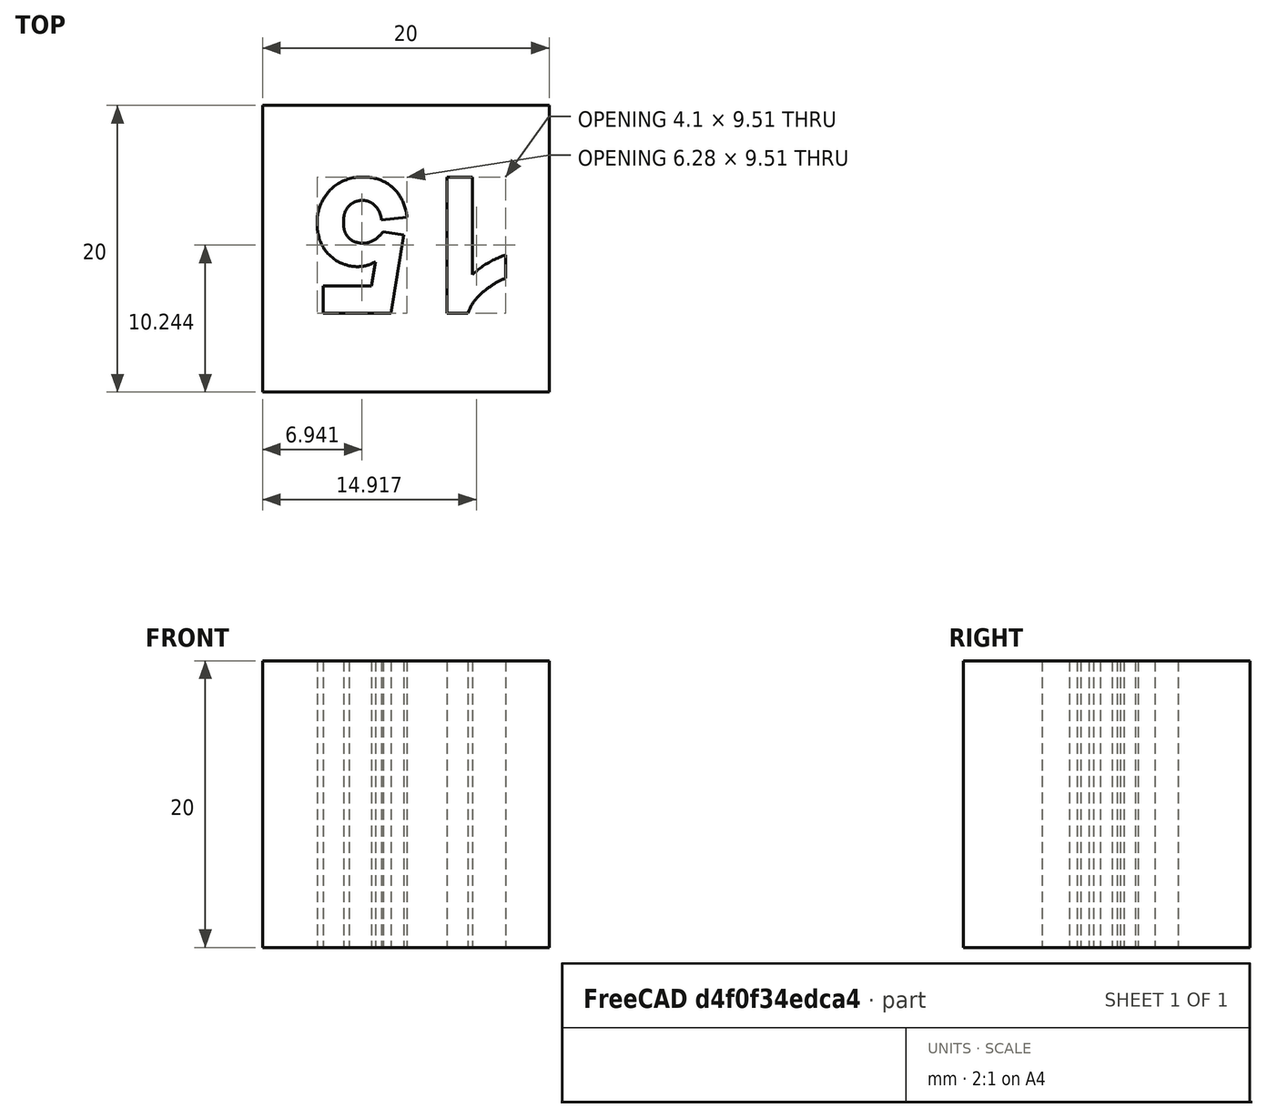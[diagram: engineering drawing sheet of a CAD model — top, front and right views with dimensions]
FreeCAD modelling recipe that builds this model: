
FCSTD DOCUMENT  (FreeCAD 0.18R16131 (Git))
Label: fill
License: All rights reserved
LicenseURL: http://en.wikipedia.org/wiki/All_rights_reserved
objects: Part::Box×1, Part::Part2DObjectPython×1, Part::Extrusion×1, Part::Cut×1
note: 4 computed .brp shape members not serialized (recipe doc carries the construction recipe); baked Part::Feature solids carry a one-line shape summary decoded from their .brp

FEATURE [Part::Box] Box  label="Cube"
  AttacherType = Attacher::AttachEngine3D
  Height = 20
  Length = 20
  Width = 20
FEATURE [Part::Part2DObjectPython] ShapeString  # Draft 2D object (typed FeaturePython)
  FontFile = <userpath>/git/aws2/bin/fonts/Arial Bold.ttf
  Placement = pos=(18,15,20) rot=(0,0,1;3.14159rad)
  Size = 10
  String = 15
  Support = -> [Box]
  Tracking = 0
FEATURE [Part::Extrusion] Extrude
  Base = -> ShapeString
  Dir = (0,0,1)
  DirMode = 2
  FaceMakerClass = Part::FaceMakerBullseye
  LengthFwd = -20
  LengthRev = 0
  Solid = false
  Symmetric = false
FEATURE [Part::Cut] Cut
  Base = -> Box
  Tool = -> Extrude
